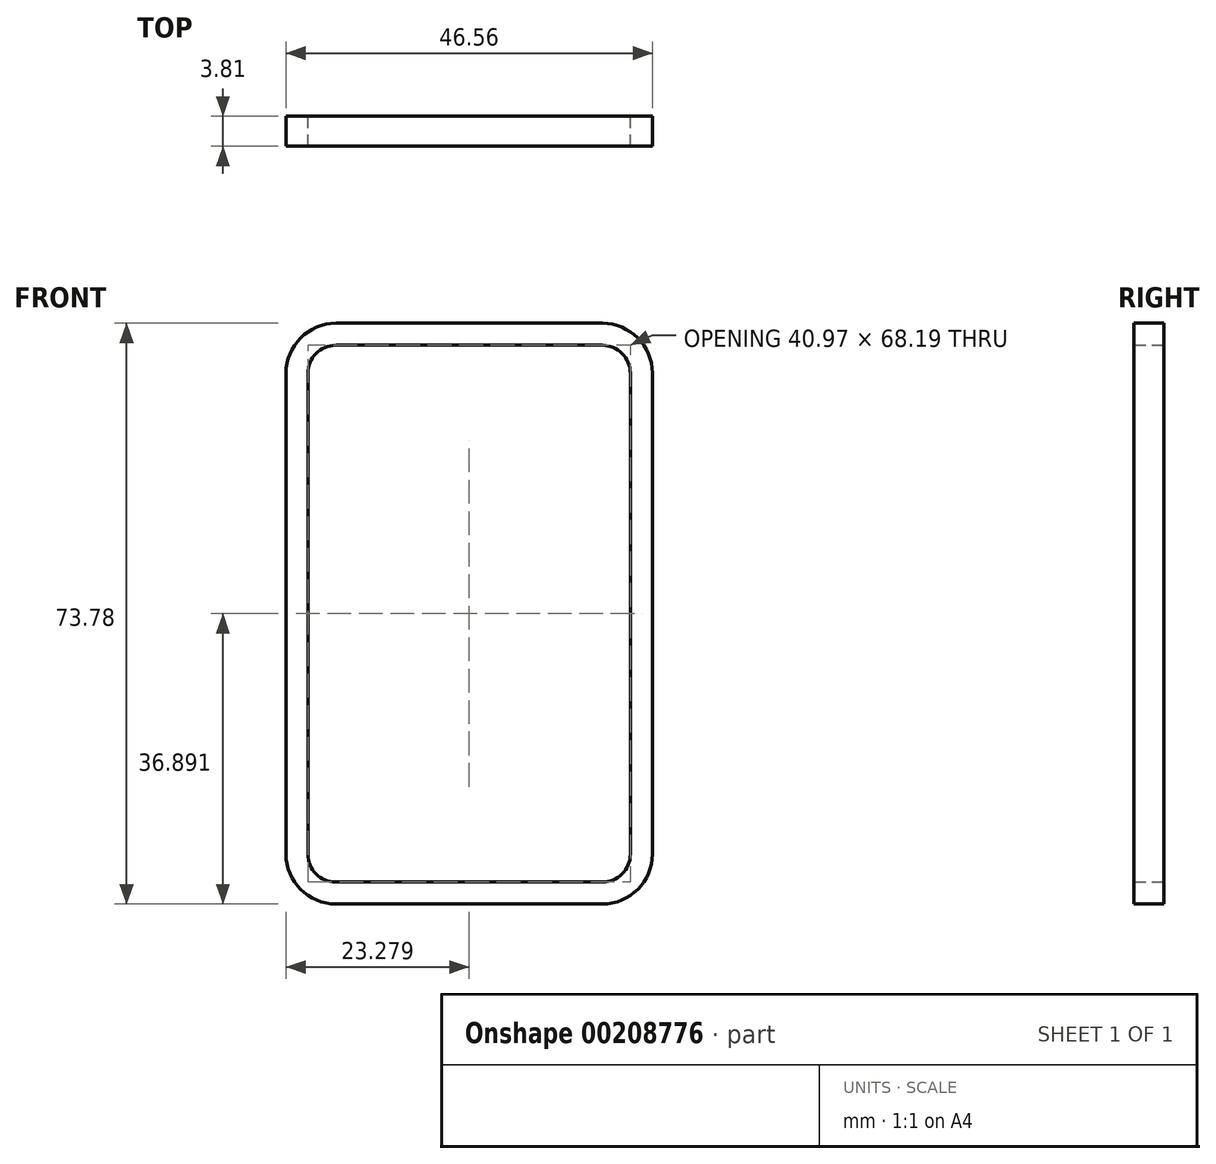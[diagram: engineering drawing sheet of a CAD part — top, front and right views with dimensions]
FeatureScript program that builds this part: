
annotation { "Feature Type Name" : "Feature", "Feature Type Description" : "" }
export const myFeature = defineFeature(function(context is Context, id is Id, definition is map)
    precondition{}
    {
        {
            var Q0;
            Q0=qCreatedBy(makeId("Front.planeOp"),FACE);
            var sketch = newSketch(context, id + "F0", { "sketchPlane" : qUnion([Q0])});
            skLineSegment(sketch, "E0.bottom", {"start": v(-17.16, 34.61) * mm, "end": v(16.7, 34.61) * mm});
            skLineSegment(sketch, "E0.top", {"start": v(-17.16, -39.17) * mm, "end": v(16.7, -39.17) * mm});
            skLineSegment(sketch, "E0.left", {"start": v(-23.5, 28.26) * mm, "end": v(-23.5, -32.82) * mm});
            skLineSegment(sketch, "E0.right", {"start": v(23.05, 28.26) * mm, "end": v(23.05, -32.82) * mm});
            skPoint(sketch, "E1.visualSharp", {"position": v(-23.5, 34.61) * mm});
            skArc(sketch, "E1.filletArc", {"start": v(-17.16, 34.61) * mm, "mid": v(-21.65, 32.75) * mm, "end": v(-23.5, 28.26) * mm});
            skPoint(sketch, "E2.visualSharp", {"position": v(23.05, 34.61) * mm});
            skArc(sketch, "E2.filletArc", {"start": v(23.05, 28.26) * mm, "mid": v(21.19, 32.75) * mm, "end": v(16.7, 34.61) * mm});
            skPoint(sketch, "E3.visualSharp", {"position": v(-23.5, -39.17) * mm});
            skArc(sketch, "E3.filletArc", {"start": v(-23.5, -32.82) * mm, "mid": v(-21.65, -37.3) * mm, "end": v(-17.16, -39.17) * mm});
            skPoint(sketch, "E4.visualSharp", {"position": v(23.05, -39.17) * mm});
            skArc(sketch, "E4.filletArc", {"start": v(16.7, -39.17) * mm, "mid": v(21.19, -37.3) * mm, "end": v(23.05, -32.82) * mm});
            skArc(sketch, "E5.0", {"start": v(-17.16, 31.82) * mm, "mid": v(-19.67, 30.77) * mm, "end": v(-20.71, 28.26) * mm});
            skLineSegment(sketch, "E5.1", {"start": v(-17.16, 31.82) * mm, "end": v(16.7, 31.82) * mm});
            skLineSegment(sketch, "E5.2", {"start": v(-20.71, 28.26) * mm, "end": v(-20.71, -32.82) * mm});
            skArc(sketch, "E5.3", {"start": v(20.25, 28.26) * mm, "mid": v(19.21, 30.77) * mm, "end": v(16.7, 31.82) * mm});
            skArc(sketch, "E5.4", {"start": v(-20.71, -32.82) * mm, "mid": v(-19.67, -35.33) * mm, "end": v(-17.16, -36.38) * mm});
            skLineSegment(sketch, "E5.5", {"start": v(-17.16, -36.38) * mm, "end": v(16.7, -36.38) * mm});
            skArc(sketch, "E5.6", {"start": v(16.7, -36.38) * mm, "mid": v(19.21, -35.33) * mm, "end": v(20.25, -32.82) * mm});
            skLineSegment(sketch, "E5.7", {"start": v(20.25, 28.26) * mm, "end": v(20.25, -32.82) * mm});
            skSolve(sketch);
        }
        {
            var Q0;
            Q0=makeQuery(id+"F0.imprint","IMPRINT",FACE,{"disambiguationData":[TD([[makeQuery(id+"F0.imprint","IMPRINT",EDGE,{"derivedFrom":sQuery(id+"F0.wireOp",EDGE,"E0.bottom")}),-1.0]])]});
            extrude(context, id + "F1", {"entities" : qUnion([Q0]), "depth" : 3.8 * mm});
        }
    });
